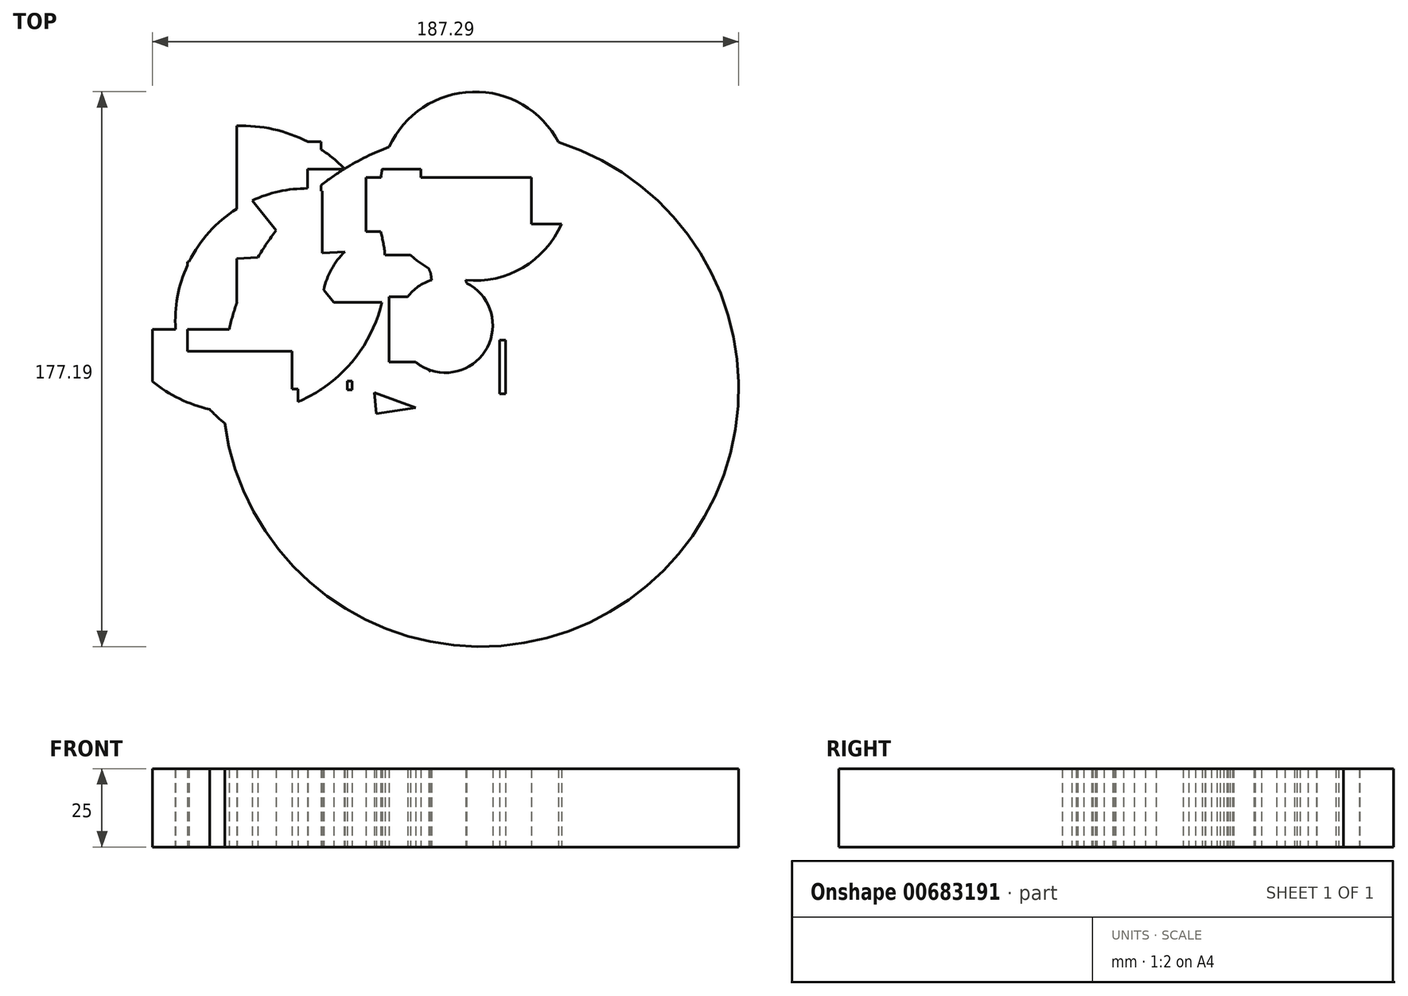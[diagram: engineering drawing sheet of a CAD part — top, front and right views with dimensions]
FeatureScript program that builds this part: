
annotation { "Feature Type Name" : "Feature", "Feature Type Description" : "" }
export const myFeature = defineFeature(function(context is Context, id is Id, definition is map)
    precondition{}
    {
        {
            var Q0;
            Q0=qCreatedBy(makeId("Top.planeOp"),FACE);
            var sketch = newSketch(context, id + "F0", { "sketchPlane" : qUnion([Q0])});
            skLineSegment(sketch, "E0.bottom", {"start": v(-76.04, 55.39) * mm, "end": v(-33.34, 55.39) * mm});
            skLineSegment(sketch, "E0.top", {"start": v(-76.04, -11.46) * mm, "end": v(-33.34, -11.46) * mm});
            skLineSegment(sketch, "E0.left", {"start": v(-76.04, 17.01) * mm, "end": v(-76.04, -11.46) * mm});
            skLineSegment(sketch, "E0.right", {"start": v(-33.34, 55.39) * mm, "end": v(-33.34, -11.46) * mm});
            skArc(sketch, "E1", {"start": v(-87.24, -21.17) * mm, "mid": v(-76.55, -27.57) * mm, "end": v(-64.54, -30.86) * mm});
            skCircle(sketch, "E2", {"center": v(15.84, 41.21) * mm, "radius": 30.15 * mm});
            skCircle(sketch, "E3", {"center": v(17.59, -23.36) * mm, "radius": 82.47 * mm});
            skArc(sketch, "E4", {"start": v(2.89, 9.71) * mm, "mid": v(-70.39, 24.98) * mm, "end": v(-40.69, -43.72) * mm});
            skArc(sketch, "E5", {"start": v(13.18, 10.26) * mm, "mid": v(-32.25, 9.06) * mm, "end": v(7.09, -13.7) * mm});
            skCircle(sketch, "E6", {"center": v(6.39, -3.24) * mm, "radius": 15.12 * mm});
            skLineSegment(sketch, "E7.bottom", {"start": v(-87.24, -4.46) * mm, "end": v(-40.69, -4.46) * mm});
            skLineSegment(sketch, "E7.top", {"start": v(-61.73, -45.94) * mm, "end": v(-40.69, -45.94) * mm});
            skLineSegment(sketch, "E7.left", {"start": v(-87.24, -4.46) * mm, "end": v(-87.24, -45.94) * mm});
            skLineSegment(sketch, "E7.right", {"start": v(-40.69, -4.46) * mm, "end": v(-40.69, -45.94) * mm});
            skLineSegment(sketch, "E8.bottom", {"start": v(-42.61, -23.54) * mm, "end": v(-32.99, -23.54) * mm});
            skLineSegment(sketch, "E8.top", {"start": v(-42.61, 39.64) * mm, "end": v(-32.99, 39.64) * mm});
            skLineSegment(sketch, "E8.left", {"start": v(-42.61, -23.54) * mm, "end": v(-42.61, 39.64) * mm});
            skLineSegment(sketch, "E8.right", {"start": v(-32.99, -23.54) * mm, "end": v(-32.99, 39.64) * mm});
            skLineSegment(sketch, "E9.bottom", {"start": v(7.09, 5.86) * mm, "end": v(-11.64, 5.86) * mm});
            skLineSegment(sketch, "E9.top", {"start": v(7.09, -14.96) * mm, "end": v(-11.64, -14.96) * mm});
            skLineSegment(sketch, "E9.left", {"start": v(7.09, 5.86) * mm, "end": v(7.09, -14.96) * mm});
            skLineSegment(sketch, "E9.right", {"start": v(-11.64, 5.86) * mm, "end": v(-11.64, -14.96) * mm});
            skLineSegment(sketch, "E10.bottom", {"start": v(-37.71, 19.16) * mm, "end": v(-1.49, 19.16) * mm});
            skLineSegment(sketch, "E10.top", {"start": v(-37.71, 46.64) * mm, "end": v(-1.49, 46.64) * mm});
            skLineSegment(sketch, "E10.left", {"start": v(-37.71, 19.16) * mm, "end": v(-37.71, 46.64) * mm});
            skLineSegment(sketch, "E10.right", {"start": v(-1.49, 19.16) * mm, "end": v(-1.49, 46.64) * mm});
            skLineSegment(sketch, "E11.bottom", {"start": v(25.64, 29.14) * mm, "end": v(48.39, 29.14) * mm});
            skLineSegment(sketch, "E11.left", {"start": v(25.64, 29.14) * mm, "end": v(25.64, 12.7) * mm});
            skLineSegment(sketch, "E11.right", {"start": v(48.39, 29.14) * mm, "end": v(48.39, -27.74) * mm});
            skLineSegment(sketch, "E12.bottom", {"start": v(2.89, 4.11) * mm, "end": v(-60.29, 4.11) * mm});
            skLineSegment(sketch, "E12.top", {"start": v(2.89, 62.74) * mm, "end": v(-5.27, 62.74) * mm});
            skLineSegment(sketch, "E12.left", {"start": v(2.89, 4.11) * mm, "end": v(2.89, 5.86) * mm});
            skLineSegment(sketch, "E12.right", {"start": v(-60.29, 4.11) * mm, "end": v(-60.29, 62.74) * mm});
            skLineSegment(sketch, "E13.bottom", {"start": v(-18.99, 44.01) * mm, "end": v(33.86, 44.01) * mm});
            skLineSegment(sketch, "E13.top", {"start": v(-18.99, 26.69) * mm, "end": v(33.86, 26.69) * mm});
            skLineSegment(sketch, "E13.left", {"start": v(-18.99, 44.01) * mm, "end": v(-18.99, 26.69) * mm});
            skLineSegment(sketch, "E13.right", {"start": v(33.86, 44.01) * mm, "end": v(33.86, 26.69) * mm});
            skLineSegment(sketch, "E14.bottom", {"start": v(48.39, -25.11) * mm, "end": v(23.71, -25.11) * mm});
            skLineSegment(sketch, "E14.top", {"start": v(25.64, -7.96) * mm, "end": v(23.71, -7.96) * mm});
            skLineSegment(sketch, "E14.left", {"start": v(48.39, -25.11) * mm, "end": v(48.39, -7.96) * mm});
            skLineSegment(sketch, "E14.right", {"start": v(23.71, -25.11) * mm, "end": v(23.71, -7.96) * mm});
            skLineSegment(sketch, "E15.bottom", {"start": v(13.39, -21.79) * mm, "end": v(7.26, -21.79) * mm});
            skLineSegment(sketch, "E15.top", {"start": v(13.39, -67.64) * mm, "end": v(7.26, -67.64) * mm});
            skLineSegment(sketch, "E15.left", {"start": v(13.39, -21.79) * mm, "end": v(13.39, -67.64) * mm});
            skLineSegment(sketch, "E15.right", {"start": v(7.26, -21.79) * mm, "end": v(7.26, -36.46) * mm});
            skLineSegment(sketch, "E16.bottom", {"start": v(-23.36, -23.89) * mm, "end": v(-24.94, -23.89) * mm});
            skLineSegment(sketch, "E16.top", {"start": v(-23.36, -21.09) * mm, "end": v(-24.94, -21.09) * mm});
            skLineSegment(sketch, "E16.left", {"start": v(-23.36, -23.89) * mm, "end": v(-23.36, -21.09) * mm});
            skLineSegment(sketch, "E16.right", {"start": v(-24.94, -23.89) * mm, "end": v(-24.94, -21.09) * mm});
            skLineSegment(sketch, "E17", {"start": v(-60.29, 42.9) * mm, "end": v(-25.99, 0) * mm});
            skLineSegment(sketch, "E18", {"start": v(-8.14, 21.44) * mm, "end": v(-99.49, 15.49) * mm});
            skLineSegment(sketch, "E19", {"start": v(0.09, 28.26) * mm, "end": v(1.98, 11.22) * mm});
            skLineSegment(sketch, "E20", {"start": v(-15.66, -31.41) * mm, "end": v(-3.06, -29.49) * mm});
            skLineSegment(sketch, "E21", {"start": v(-3.06, -29.49) * mm, "end": v(-16.36, -24.76) * mm});
            skLineSegment(sketch, "E22", {"start": v(-16.36, -24.76) * mm, "end": v(-15.66, -31.41) * mm});
            skArc(sketch, "E23.trimOffspring", {"start": v(-40.69, -27.64) * mm, "mid": v(-13.76, 24.57) * mm, "end": v(-60.29, 60.45) * mm});
            skLineSegment(sketch, "E24.trimOffspring", {"start": v(4.05, -7.47) * mm, "end": v(8.49, -47.51) * mm});
            skLineSegment(sketch, "E25.trimOffspring", {"start": v(2.89, 9.71) * mm, "end": v(2.89, 62.74) * mm});
            skLineSegment(sketch, "E26.trimOffspring", {"start": v(2.57, 5.86) * mm, "end": v(2.76, 4.11) * mm});
            skLineSegment(sketch, "E27.trimOffspring", {"start": v(25.64, -7.96) * mm, "end": v(25.64, -27.74) * mm});
            skArc(sketch, "E28.trimOffspring", {"start": v(-6.5, -30.01) * mm, "mid": v(0.47, -19.54) * mm, "end": v(4.05, -7.47) * mm});
            skSolve(sketch);
        }
        {
            var Q0;
            {var subQ0=sQuery(id+"F0.wireOp",EDGE,"E12.right");var subQ1=sQuery(id+"F0.wireOp",EDGE,"E0.bottom");var subQ2=makeQuery(id+"F0.imprint","INTERSECT",VERTEX,{"derivedFrom":[subQ1,subQ0]});Q0=makeQuery(id+"F0.imprint","IMPRINT",FACE,{"disambiguationData":[TD([[makeQuery(id+"F0.imprint","IMPRINT",EDGE,{"disambiguationData":[TD([[subQ2,-1.0]])],"derivedFrom":subQ1}),1.0]])]});}
            var Q1;
            {var subQ0=sQuery(id+"F0.wireOp",EDGE,"E0.right");var subQ1=sQuery(id+"F0.wireOp",EDGE,"E0.bottom");var subQ2=makeQuery(id+"F0.imprint","INTERSECT",VERTEX,{"derivedFrom":[subQ1,subQ0]});Q1=makeQuery(id+"F0.imprint","IMPRINT",FACE,{"disambiguationData":[TD([[makeQuery(id+"F0.imprint","IMPRINT",EDGE,{"disambiguationData":[TD([[subQ2,1.0]])],"derivedFrom":subQ1}),-1.0]])]});}
            var Q2;
            {var subQ0=sQuery(id+"F0.wireOp",EDGE,"E18");var subQ1=sQuery(id+"F0.wireOp",EDGE,"E0.left");var subQ2=makeQuery(id+"F0.imprint","INTERSECT",VERTEX,{"derivedFrom":[subQ1,subQ0]});Q2=makeQuery(id+"F0.imprint","IMPRINT",FACE,{"disambiguationData":[TD([[makeQuery(id+"F0.imprint","IMPRINT",EDGE,{"disambiguationData":[TD([[subQ2,-1.0]])],"derivedFrom":subQ1}),1.0]])]});}
            var Q3;
            {var subQ0=sQuery(id+"F0.wireOp",EDGE,"E7.left");var subQ1=sQuery(id+"F0.wireOp",EDGE,"E1");var subQ2=makeQuery(id+"F0.imprint","INTERSECT",VERTEX,{"derivedFrom":[subQ1,subQ0]});Q3=makeQuery(id+"F0.imprint","IMPRINT",FACE,{"disambiguationData":[TD([[makeQuery(id+"F0.imprint","IMPRINT",EDGE,{"disambiguationData":[TD([[subQ2,-1.0]])],"derivedFrom":subQ1}),1.0]])]});}
            var Q4;
            {var subQ0=sQuery(id+"F0.wireOp",EDGE,"E4");var subQ1=sQuery(id+"F0.wireOp",EDGE,"E0.left");var subQ2=makeQuery(id+"F0.imprint","INTERSECT",VERTEX,{"derivedFrom":[subQ1,subQ0]});Q4=makeQuery(id+"F0.imprint","IMPRINT",FACE,{"disambiguationData":[TD([[makeQuery(id+"F0.imprint","IMPRINT",EDGE,{"disambiguationData":[TD([[subQ2,-1.0]])],"derivedFrom":subQ1}),-1.0]])]});}
            var Q5;
            {var subQ0=sQuery(id+"F0.wireOp",EDGE,"E3");var subQ1=sQuery(id+"F0.wireOp",EDGE,"E1");var subQ2=makeQuery(id+"F0.imprint","INTERSECT",VERTEX,{"derivedFrom":[subQ1,subQ0]});Q5=makeQuery(id+"F0.imprint","IMPRINT",FACE,{"disambiguationData":[TD([[makeQuery(id+"F0.imprint","IMPRINT",EDGE,{"disambiguationData":[TD([[subQ2,1.0]])],"derivedFrom":subQ1}),-1.0]])]});}
            var Q6;
            {var subQ0=sQuery(id+"F0.wireOp",EDGE,"E12.top");Q6=makeQuery(id+"F0.imprint","IMPRINT",FACE,{"disambiguationData":[TD([[makeQuery(id+"F0.imprint","IMPRINT",EDGE,{"derivedFrom":subQ0}),-1.0]])]});}
            var Q7;
            {var subQ0=sQuery(id+"F0.wireOp",EDGE,"E12.top");Q7=makeQuery(id+"F0.imprint","IMPRINT",FACE,{"disambiguationData":[TD([[makeQuery(id+"F0.imprint","IMPRINT",EDGE,{"derivedFrom":subQ0}),1.0]])]});}
            var Q8;
            {var subQ0=sQuery(id+"F0.wireOp",EDGE,"E7.top");Q8=makeQuery(id+"F0.imprint","IMPRINT",FACE,{"disambiguationData":[TD([[makeQuery(id+"F0.imprint","IMPRINT",EDGE,{"derivedFrom":subQ0}),1.0]])]});}
            var Q9;
            {var subQ0=sQuery(id+"F0.wireOp",EDGE,"E12.right");var subQ1=sQuery(id+"F0.wireOp",EDGE,"E4");var subQ2=makeQuery(id+"F0.imprint","INTERSECT",VERTEX,{"derivedFrom":[subQ1,subQ0]});Q9=makeQuery(id+"F0.imprint","IMPRINT",FACE,{"disambiguationData":[TD([[makeQuery(id+"F0.imprint","IMPRINT",EDGE,{"disambiguationData":[TD([[subQ2,1.0]])],"derivedFrom":subQ1}),-1.0]])]});}
            var Q10;
            {var subQ0=sQuery(id+"F0.wireOp",EDGE,"E12.right");var subQ1=sQuery(id+"F0.wireOp",EDGE,"E4");var subQ2=makeQuery(id+"F0.imprint","INTERSECT",VERTEX,{"derivedFrom":[subQ1,subQ0]});Q10=makeQuery(id+"F0.imprint","IMPRINT",FACE,{"disambiguationData":[TD([[makeQuery(id+"F0.imprint","IMPRINT",EDGE,{"disambiguationData":[TD([[subQ2,-1.0]])],"derivedFrom":subQ1}),1.0]])]});}
            var Q11;
            {var subQ0=sQuery(id+"F0.wireOp",EDGE,"E23.trimOffspring");var subQ1=sQuery(id+"F0.wireOp",EDGE,"E0.right");var subQ2=makeQuery(id+"F0.imprint","INTERSECT",VERTEX,{"derivedFrom":[subQ1,subQ0]});Q11=makeQuery(id+"F0.imprint","IMPRINT",FACE,{"disambiguationData":[TD([[makeQuery(id+"F0.imprint","IMPRINT",EDGE,{"disambiguationData":[TD([[subQ2,-1.0]])],"derivedFrom":subQ1}),1.0]])]});}
            var Q12;
            {var subQ0=sQuery(id+"F0.wireOp",EDGE,"E3");var subQ1=sQuery(id+"F0.wireOp",EDGE,"E2");var subQ2=makeQuery(id+"F0.imprint","INTERSECT",VERTEX,{"disambiguationData":[OD(1.0)],"derivedFrom":[subQ1,subQ0]});Q12=makeQuery(id+"F0.imprint","IMPRINT",FACE,{"disambiguationData":[TD([[makeQuery(id+"F0.imprint","IMPRINT",EDGE,{"disambiguationData":[TD([[subQ2,-1.0]])],"derivedFrom":subQ1}),-1.0]])]});}
            var Q13;
            {var subQ0=sQuery(id+"F0.wireOp",EDGE,"E23.trimOffspring");var subQ1=sQuery(id+"F0.wireOp",EDGE,"E3");var subQ2=makeQuery(id+"F0.imprint","INTERSECT",VERTEX,{"derivedFrom":[subQ1,subQ0]});Q13=makeQuery(id+"F0.imprint","IMPRINT",FACE,{"disambiguationData":[TD([[makeQuery(id+"F0.imprint","IMPRINT",EDGE,{"disambiguationData":[TD([[subQ2,-1.0]])],"derivedFrom":subQ1}),1.0]])]});}
            var Q14;
            {var subQ3=sQuery(id+"F0.wireOp",EDGE,"E0.top");var subQ7=sQuery(id+"F0.wireOp",EDGE,"E0.left");var subQ8=makeQuery(id+"F0.imprint","INTERSECT",VERTEX,{"derivedFrom":[subQ3,subQ7]});Q14=makeQuery(id+"F0.imprint","IMPRINT",FACE,{"disambiguationData":[TD([[makeQuery(id+"F0.imprint","IMPRINT",EDGE,{"disambiguationData":[TD([[subQ8,-1.0]])],"derivedFrom":subQ3}),-1.0]])]});}
            var Q15;
            {var subQ0=sQuery(id+"F0.wireOp",EDGE,"E3");var subQ1=sQuery(id+"F0.wireOp",EDGE,"E2");var subQ2=makeQuery(id+"F0.imprint","INTERSECT",VERTEX,{"disambiguationData":[OD(1.0)],"derivedFrom":[subQ1,subQ0]});Q15=makeQuery(id+"F0.imprint","IMPRINT",FACE,{"disambiguationData":[TD([[makeQuery(id+"F0.imprint","IMPRINT",EDGE,{"disambiguationData":[TD([[subQ2,-1.0]])],"derivedFrom":subQ1}),1.0]])]});}
            var Q16;
            {var subQ5=sQuery(id+"F0.wireOp",EDGE,"E3");var subQ6=sQuery(id+"F0.wireOp",EDGE,"E2");var subQ7=makeQuery(id+"F0.imprint","INTERSECT",VERTEX,{"disambiguationData":[OD(0.0)],"derivedFrom":[subQ6,subQ5]});Q16=makeQuery(id+"F0.imprint","IMPRINT",FACE,{"disambiguationData":[TD([[makeQuery(id+"F0.imprint","IMPRINT",EDGE,{"disambiguationData":[TD([[subQ7,1.0]])],"derivedFrom":subQ6}),1.0]])]});}
            var Q17;
            {var subQ0=sQuery(id+"F0.wireOp",EDGE,"E17");var subQ1=sQuery(id+"F0.wireOp",EDGE,"E3");var subQ2=makeQuery(id+"F0.imprint","INTERSECT",VERTEX,{"derivedFrom":[subQ1,subQ0]});Q17=makeQuery(id+"F0.imprint","IMPRINT",FACE,{"disambiguationData":[TD([[makeQuery(id+"F0.imprint","IMPRINT",EDGE,{"disambiguationData":[TD([[subQ2,-1.0]])],"derivedFrom":subQ1}),-1.0]])]});}
            var Q18;
            {var subQ9=sQuery(id+"F0.wireOp",EDGE,"E12.right");var subQ10=sQuery(id+"F0.wireOp",EDGE,"E0.bottom");var subQ11=makeQuery(id+"F0.imprint","INTERSECT",VERTEX,{"derivedFrom":[subQ10,subQ9]});Q18=makeQuery(id+"F0.imprint","IMPRINT",FACE,{"disambiguationData":[TD([[makeQuery(id+"F0.imprint","IMPRINT",EDGE,{"disambiguationData":[TD([[subQ11,-1.0]])],"derivedFrom":subQ10}),-1.0]])]});}
            var Q19;
            {var subQ1=sQuery(id+"F0.wireOp",EDGE,"E0.left");var subQ5=sQuery(id+"F0.wireOp",EDGE,"E4");var subQ6=makeQuery(id+"F0.imprint","INTERSECT",VERTEX,{"derivedFrom":[subQ1,subQ5]});Q19=makeQuery(id+"F0.imprint","IMPRINT",FACE,{"disambiguationData":[TD([[makeQuery(id+"F0.imprint","IMPRINT",EDGE,{"disambiguationData":[TD([[subQ6,-1.0]])],"derivedFrom":subQ1}),1.0]])]});}
            var Q20;
            {var subQ0=sQuery(id+"F0.wireOp",EDGE,"E3");var subQ6=sQuery(id+"F0.wireOp",EDGE,"E0.top");var subQ7=makeQuery(id+"F0.imprint","INTERSECT",VERTEX,{"derivedFrom":[subQ6,subQ0]});Q20=makeQuery(id+"F0.imprint","IMPRINT",FACE,{"disambiguationData":[TD([[makeQuery(id+"F0.imprint","IMPRINT",EDGE,{"disambiguationData":[TD([[subQ7,-1.0]])],"derivedFrom":subQ6}),-1.0]])]});}
            var Q21;
            {var subQ21=sQuery(id+"F0.wireOp",EDGE,"E7.top");Q21=makeQuery(id+"F0.imprint","IMPRINT",FACE,{"disambiguationData":[TD([[makeQuery(id+"F0.imprint","IMPRINT",EDGE,{"derivedFrom":subQ21}),-1.0]])]});}
            var Q22;
            {var subQ7=sQuery(id+"F0.wireOp",EDGE,"E28.trimOffspring");var subQ9=sQuery(id+"F0.wireOp",EDGE,"E5");var subQ10=makeQuery(id+"F0.imprint","INTERSECT",VERTEX,{"derivedFrom":[subQ9,subQ7]});Q22=makeQuery(id+"F0.imprint","IMPRINT",FACE,{"disambiguationData":[TD([[makeQuery(id+"F0.imprint","IMPRINT",EDGE,{"disambiguationData":[TD([[subQ10,1.0]])],"derivedFrom":subQ9}),1.0]])]});}
            var Q23;
            {var subQ3=sQuery(id+"F0.wireOp",EDGE,"E5");var subQ7=sQuery(id+"F0.wireOp",EDGE,"E10.bottom");var subQ8=makeQuery(id+"F0.imprint","INTERSECT",VERTEX,{"derivedFrom":[subQ3,subQ7]});Q23=makeQuery(id+"F0.imprint","IMPRINT",FACE,{"disambiguationData":[TD([[makeQuery(id+"F0.imprint","IMPRINT",EDGE,{"disambiguationData":[TD([[subQ8,-1.0]])],"derivedFrom":subQ3}),1.0]])]});}
            var Q24;
            {var subQ3=sQuery(id+"F0.wireOp",EDGE,"E0.right");var subQ11=sQuery(id+"F0.wireOp",EDGE,"E4");var subQ12=makeQuery(id+"F0.imprint","INTERSECT",VERTEX,{"derivedFrom":[subQ3,subQ11]});Q24=makeQuery(id+"F0.imprint","IMPRINT",FACE,{"disambiguationData":[TD([[makeQuery(id+"F0.imprint","IMPRINT",EDGE,{"disambiguationData":[TD([[subQ12,-1.0]])],"derivedFrom":subQ3}),1.0]])]});}
            var Q25;
            {var subQ0=sQuery(id+"F0.wireOp",EDGE,"E18");var subQ1=sQuery(id+"F0.wireOp",EDGE,"E5");var subQ2=makeQuery(id+"F0.imprint","INTERSECT",VERTEX,{"derivedFrom":[subQ1,subQ0]});Q25=makeQuery(id+"F0.imprint","IMPRINT",FACE,{"disambiguationData":[TD([[makeQuery(id+"F0.imprint","IMPRINT",EDGE,{"disambiguationData":[TD([[subQ2,-1.0]])],"derivedFrom":subQ1}),1.0]])]});}
            var Q26;
            {var subQ1=sQuery(id+"F0.wireOp",EDGE,"E3");var subQ6=sQuery(id+"F0.wireOp",EDGE,"E0.right");var subQ11=makeQuery(id+"F0.imprint","INTERSECT",VERTEX,{"derivedFrom":[subQ6,subQ1]});Q26=makeQuery(id+"F0.imprint","IMPRINT",FACE,{"disambiguationData":[TD([[makeQuery(id+"F0.imprint","IMPRINT",EDGE,{"disambiguationData":[TD([[subQ11,-1.0]])],"derivedFrom":subQ6}),1.0]])]});}
            var Q27;
            {var subQ5=sQuery(id+"F0.wireOp",EDGE,"E2");var subQ7=sQuery(id+"F0.wireOp",EDGE,"E10.top");var subQ8=makeQuery(id+"F0.imprint","INTERSECT",VERTEX,{"derivedFrom":[subQ5,subQ7]});Q27=makeQuery(id+"F0.imprint","IMPRINT",FACE,{"disambiguationData":[TD([[makeQuery(id+"F0.imprint","IMPRINT",EDGE,{"disambiguationData":[TD([[subQ8,-1.0]])],"derivedFrom":subQ5}),-1.0]])]});}
            var Q28;
            {var subQ0=sQuery(id+"F0.wireOp",EDGE,"E23.trimOffspring");var subQ1=sQuery(id+"F0.wireOp",EDGE,"E5");var subQ2=makeQuery(id+"F0.imprint","INTERSECT",VERTEX,{"disambiguationData":[OD(0.0)],"derivedFrom":[subQ1,subQ0]});Q28=makeQuery(id+"F0.imprint","IMPRINT",FACE,{"disambiguationData":[TD([[makeQuery(id+"F0.imprint","IMPRINT",EDGE,{"disambiguationData":[TD([[subQ2,-1.0]])],"derivedFrom":subQ1}),1.0]])]});}
            var Q29;
            {var subQ6=sQuery(id+"F0.wireOp",EDGE,"E10.bottom");var subQ13=sQuery(id+"F0.wireOp",EDGE,"E2");var subQ16=makeQuery(id+"F0.imprint","INTERSECT",VERTEX,{"derivedFrom":[subQ13,subQ6]});Q29=makeQuery(id+"F0.imprint","IMPRINT",FACE,{"disambiguationData":[TD([[makeQuery(id+"F0.imprint","IMPRINT",EDGE,{"disambiguationData":[TD([[subQ16,-1.0]])],"derivedFrom":subQ13}),-1.0]])]});}
            extrude(context, id + "F1", {"entities" : qUnion([Q0, Q1, Q2, Q3, Q4, Q5, Q6, Q7, Q8, Q9, Q10, Q11, Q12, Q13, Q14, Q15, Q16, Q17, Q18, Q19, Q20, Q21, Q22, Q23, Q24, Q25, Q26, Q27, Q28, Q29]), "depth" : 25 * mm, "offsetDistance" : 25 * mm});
        }
    });
